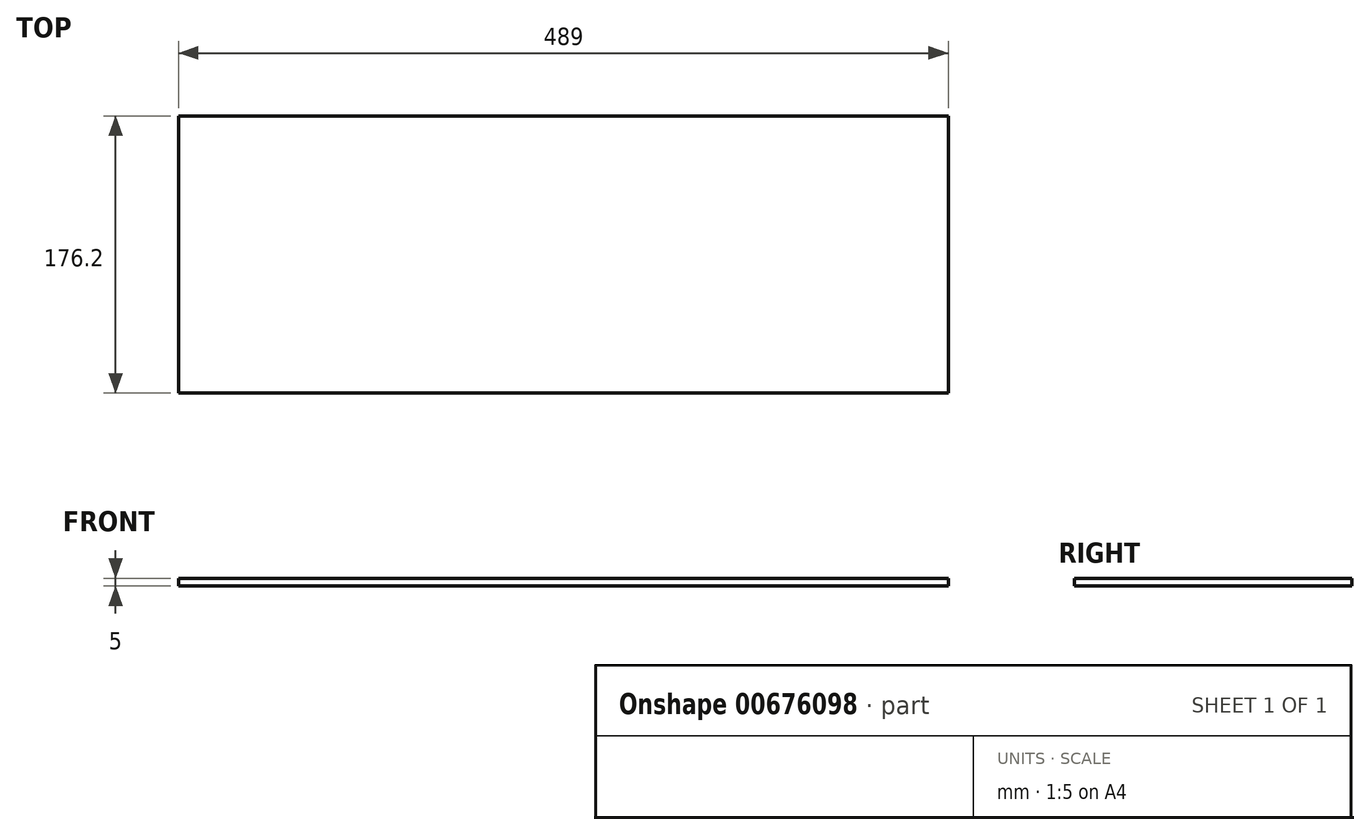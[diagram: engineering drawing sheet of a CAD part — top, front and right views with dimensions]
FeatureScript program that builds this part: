
annotation { "Feature Type Name" : "Feature", "Feature Type Description" : "" }
export const myFeature = defineFeature(function(context is Context, id is Id, definition is map)
    precondition{}
    {
        {
            var Q0;
            Q0=qCreatedBy(makeId("Front.planeOp"),FACE);
            var sketch = newSketch(context, id + "F0", { "sketchPlane" : qUnion([Q0])});
            skLineSegment(sketch, "E0.bottom", {"start": v(244.5, 2.5) * mm, "end": v(-244.5, 2.5) * mm});
            skLineSegment(sketch, "E0.top", {"start": v(244.5, -2.5) * mm, "end": v(-244.5, -2.5) * mm});
            skLineSegment(sketch, "E0.left", {"start": v(244.5, 2.5) * mm, "end": v(244.5, -2.5) * mm});
            skLineSegment(sketch, "E0.right", {"start": v(-244.5, 2.5) * mm, "end": v(-244.5, -2.5) * mm});
            skPoint(sketch, "E0.middle", {"position": v(0, 0) * mm});
            skSolve(sketch);
        }
        {
            var Q0;
            Q0 = qSketchRegion(id + "F0", true);
            extrude(context, id + "F1", {"entities" : qUnion([Q0]), "depth" : 176.2 * mm, "offsetDistance" : 25 * mm});
        }
    });
